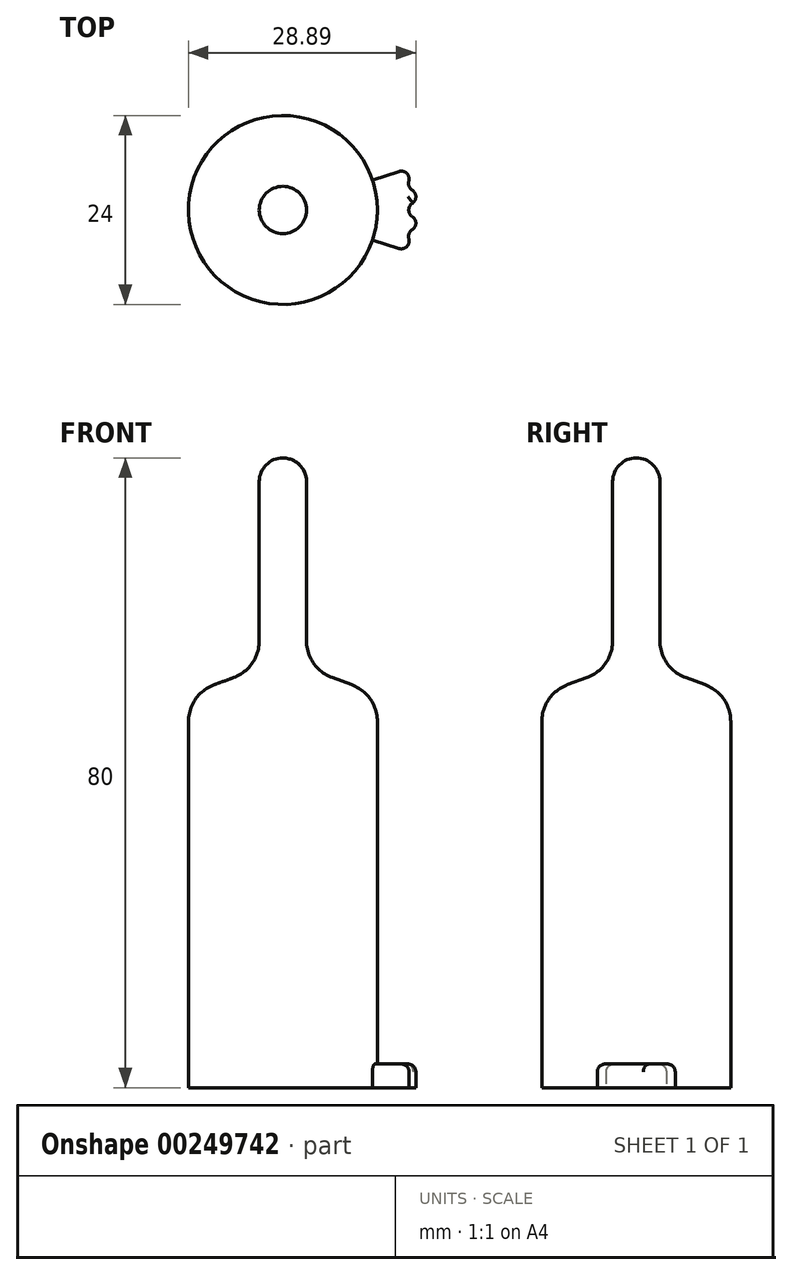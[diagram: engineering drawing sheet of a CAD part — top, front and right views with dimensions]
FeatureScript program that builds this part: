
annotation { "Feature Type Name" : "Feature", "Feature Type Description" : "" }
export const myFeature = defineFeature(function(context is Context, id is Id, definition is map)
    precondition{}
    {
        {
            var Q0;
            Q0=qCreatedBy(makeId("Front.planeOp"),FACE);
            var sketch = newSketch(context, id + "F0", { "sketchPlane" : qUnion([Q0])});
            skLineSegment(sketch, "E0", {"start": v(0, 0) * mm, "end": v(12, 0) * mm});
            skLineSegment(sketch, "E1", {"start": v(12, 0) * mm, "end": v(12, 50) * mm});
            skLineSegment(sketch, "E2", {"start": v(12, 50) * mm, "end": v(3, 53.28) * mm});
            skLineSegment(sketch, "E3", {"start": v(3, 53.28) * mm, "end": v(3, 77) * mm});
            skLineSegment(sketch, "E4", {"start": v(0, 0) * mm, "end": v(0, 77) * mm});
            skArc(sketch, "E5", {"start": v(3, 77) * mm, "mid": v(2.12, 79.12) * mm, "end": v(0, 80) * mm});
            skLineSegment(sketch, "E6", {"start": v(0, 77) * mm, "end": v(0, 80) * mm});
            skLineSegment(sketch, "E7", {"start": v(0, 77) * mm, "end": v(3, 77) * mm, "construction": true});
            skSolve(sketch);
        }
        {
            var Q0;
            Q0=makeQuery(id+"F0.imprint","IMPRINT",FACE,{"disambiguationData":[TD([[makeQuery(id+"F0.imprint","IMPRINT",EDGE,{"derivedFrom":sQuery(id+"F0.wireOp",EDGE,"E0")}),1.0]])]});
            var Q1;
            Q1=sQuery(id+"F0.wireOp",EDGE,"E4");
            revolve(context, id + "F1", {"entities" : qUnion([Q0]), "axis" : qUnion([Q1]), "revolveType" : RevolveType.FULL});
        }
        {
            var Q0;
            Q0=makeQuery(id+"F1.opRevolve","SWEPT_FACE",FACE,{"disambiguationData":[OSD([sQuery(id+"F0.wireOp",EDGE,"E0")])]});
            var sketch = newSketch(context, id + "F2", { "sketchPlane" : qUnion([Q0])});
            skLineSegment(sketch, "E8", {"start": v(0, 0) * mm, "end": v(33.6, -33.6) * mm, "construction": true});
            skLineSegment(sketch, "E9", {"start": v(15.37, 0) * mm, "end": v(17.7, -1.83) * mm});
            skLineSegment(sketch, "E10", {"start": v(17.7, -1.83) * mm, "end": v(15.43, -3.06) * mm});
            skLineSegment(sketch, "E11", {"start": v(15.43, -3.06) * mm, "end": v(17.64, -5.83) * mm});
            skLineSegment(sketch, "E12", {"start": v(17.64, -5.83) * mm, "end": v(11.38, -3.82) * mm});
            skLineSegment(sketch, "E13", {"start": v(12, 0) * mm, "end": v(15.37, 0) * mm, "construction": true});
            skLineSegment(sketch, "E14.MirrorCS", {"start": v(15.43, 3.06) * mm, "end": v(17.64, 5.83) * mm});
            skLineSegment(sketch, "E15.MirrorCS", {"start": v(17.7, 1.83) * mm, "end": v(15.43, 3.06) * mm});
            skLineSegment(sketch, "E16.MirrorCS", {"start": v(17.64, 5.83) * mm, "end": v(11.38, 3.82) * mm});
            skLineSegment(sketch, "E17.MirrorCS", {"start": v(15.37, 0) * mm, "end": v(17.7, 1.83) * mm});
            skSolve(sketch);
        }
        {
            var Q0;
            Q0=makeQuery(id+"F2.imprint","IMPRINT",FACE,{"disambiguationData":[TD([[makeQuery(id+"F2.imprint","IMPRINT",EDGE,{"derivedFrom":sQuery(id+"F2.wireOp",EDGE,"E9")}),-1.0]])]});
            extrude(context, id + "F3", {"entities" : qUnion([Q0]), "operationType" : NewBodyOperationType.ADD, "oppositeDirection" : true, "depth" : 3 * mm});
        }
        {
            var Q0;
            Q0=makeQuery(id+"F3.opExtrude","SWEPT_EDGE",EDGE,{"disambiguationData":[OSD([sQuery(id+"F0.wireOp",EDGE,"E0"),sQuery(id+"F0.wireOp",EDGE,"E1"),sQuery(id+"F2.wireOp",EDGE,"E16.MirrorCS")])]});
            var Q1;
            Q1=makeQuery(id+"F3.opExtrude","SWEPT_EDGE",EDGE,{"disambiguationData":[OSD([sQuery(id+"F0.wireOp",EDGE,"E0"),sQuery(id+"F0.wireOp",EDGE,"E1"),sQuery(id+"F2.wireOp",EDGE,"E12")])]});
            var Q2;
            Q2=makeQuery(id+"F3.opExtrude","CAP_EDGE",EDGE,{"disambiguationData":[OSD([sQuery(id+"F0.wireOp",EDGE,"E0"),sQuery(id+"F0.wireOp",EDGE,"E1")])],"isStart":false});
            var Q3;
            Q3=makeQuery(id+"F3.opExtrude","CAP_EDGE",EDGE,{"disambiguationData":[OSD([sQuery(id+"F2.wireOp",EDGE,"E16.MirrorCS")])],"isStart":false});
            var Q4;
            Q4=makeQuery(id+"F3.opExtrude","CAP_EDGE",EDGE,{"disambiguationData":[OSD([sQuery(id+"F2.wireOp",EDGE,"E12")])],"isStart":false});
            var Q5;
            Q5=makeQuery(id+"F3.opExtrude","CAP_EDGE",EDGE,{"disambiguationData":[OSD([sQuery(id+"F2.wireOp",EDGE,"E10")])],"isStart":false});
            var Q6;
            Q6=makeQuery(id+"F3.opExtrude","CAP_EDGE",EDGE,{"disambiguationData":[OSD([sQuery(id+"F2.wireOp",EDGE,"E11")])],"isStart":false});
            var Q7;
            Q7=makeQuery(id+"F3.opExtrude","CAP_EDGE",EDGE,{"disambiguationData":[OSD([sQuery(id+"F2.wireOp",EDGE,"E9")])],"isStart":false});
            var Q8;
            Q8=makeQuery(id+"F3.opExtrude","CAP_EDGE",EDGE,{"disambiguationData":[OSD([sQuery(id+"F2.wireOp",EDGE,"E17.MirrorCS")])],"isStart":false});
            var Q9;
            Q9=makeQuery(id+"F3.opExtrude","CAP_EDGE",EDGE,{"disambiguationData":[OSD([sQuery(id+"F2.wireOp",EDGE,"E15.MirrorCS")])],"isStart":false});
            var Q10;
            Q10=makeQuery(id+"F3.opExtrude","CAP_EDGE",EDGE,{"disambiguationData":[OSD([sQuery(id+"F2.wireOp",EDGE,"E14.MirrorCS")])],"isStart":false});
            var Q11;
            Q11=makeQuery(id+"F3.opExtrude","SWEPT_EDGE",EDGE,{"disambiguationData":[OSD([sQuery(id+"F2.wireOp",EDGE,"E14.MirrorCS"),sQuery(id+"F2.wireOp",EDGE,"E15.MirrorCS")])]});
            var Q12;
            Q12=makeQuery(id+"F3.opExtrude","SWEPT_EDGE",EDGE,{"disambiguationData":[OSD([sQuery(id+"F2.wireOp",EDGE,"E9"),sQuery(id+"F2.wireOp",EDGE,"E17.MirrorCS")])]});
            var Q13;
            Q13=makeQuery(id+"F3.opExtrude","SWEPT_EDGE",EDGE,{"disambiguationData":[OSD([sQuery(id+"F2.wireOp",EDGE,"E10"),sQuery(id+"F2.wireOp",EDGE,"E11")])]});
            fillet(context, id + "F4", {"entities" : qUnion([Q0, Q1, Q2, Q3, Q4, Q5, Q6, Q7, Q8, Q9, Q10, Q11, Q12, Q13]), "radius" : 1 * mm, "tangentPropagation" : true, "allowEdgeOverflow" : false});
        }
        {
            var Q0;
            Q0=makeQuery(id+"F3.opExtrude","SWEPT_EDGE",EDGE,{"disambiguationData":[OSD([sQuery(id+"F2.wireOp",EDGE,"E14.MirrorCS"),sQuery(id+"F2.wireOp",EDGE,"E16.MirrorCS")])]});
            var Q1;
            Q1=makeQuery(id+"F3.opExtrude","SWEPT_EDGE",EDGE,{"disambiguationData":[OSD([sQuery(id+"F2.wireOp",EDGE,"E15.MirrorCS"),sQuery(id+"F2.wireOp",EDGE,"E17.MirrorCS")])]});
            var Q2;
            Q2=makeQuery(id+"F3.opExtrude","SWEPT_EDGE",EDGE,{"disambiguationData":[OSD([sQuery(id+"F2.wireOp",EDGE,"E9"),sQuery(id+"F2.wireOp",EDGE,"E10")])]});
            var Q3;
            Q3=makeQuery(id+"F3.opExtrude","SWEPT_EDGE",EDGE,{"disambiguationData":[OSD([sQuery(id+"F2.wireOp",EDGE,"E11"),sQuery(id+"F2.wireOp",EDGE,"E12")])]});
            fillet(context, id + "F5", {"entities" : qUnion([Q0, Q1, Q2, Q3]), "radius" : 1 * mm, "tangentPropagation" : true, "allowEdgeOverflow" : false});
        }
        {
            var Q0;
            Q0=makeQuery(id+"F1.opRevolve","SWEPT_EDGE",EDGE,{"disambiguationData":[OSD([sQuery(id+"F0.wireOp",EDGE,"E2"),sQuery(id+"F0.wireOp",EDGE,"E3")])]});
            var Q1;
            Q1=makeQuery(id+"F1.opRevolve","SWEPT_EDGE",EDGE,{"disambiguationData":[OSD([sQuery(id+"F0.wireOp",EDGE,"E1"),sQuery(id+"F0.wireOp",EDGE,"E2")])]});
            fillet(context, id + "F6", {"entities" : qUnion([Q0, Q1]), "radius" : 5 * mm, "tangentPropagation" : true, "allowEdgeOverflow" : false});
        }
    });
